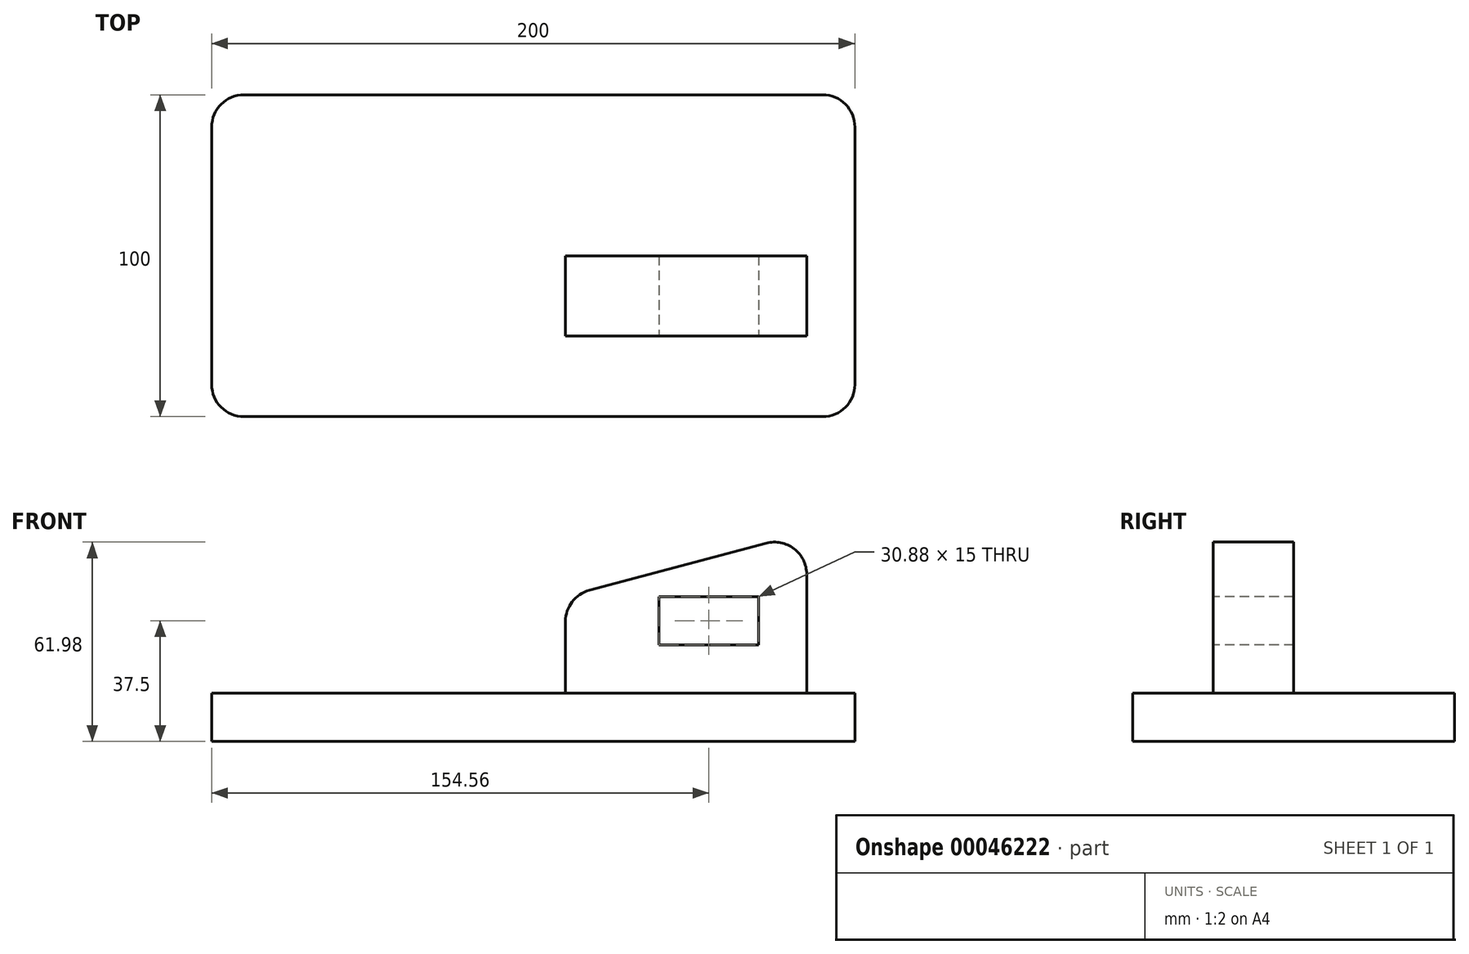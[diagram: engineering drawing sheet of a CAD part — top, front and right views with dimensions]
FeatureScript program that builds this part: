
annotation { "Feature Type Name" : "Feature", "Feature Type Description" : "" }
export const myFeature = defineFeature(function(context is Context, id is Id, definition is map)
    precondition{}
    {
        {
            var Q0;
            Q0=qCreatedBy(makeId("Top.planeOp"),FACE);
            var sketch = newSketch(context, id + "F0", { "sketchPlane" : qUnion([Q0])});
            skLineSegment(sketch, "E0.rect.bottom", {"start": v(100, 50) * mm, "end": v(-100, 50) * mm});
            skLineSegment(sketch, "E0.rect.top", {"start": v(100, -50) * mm, "end": v(-100, -50) * mm});
            skLineSegment(sketch, "E0.rect.left", {"start": v(100, 50) * mm, "end": v(100, -50) * mm});
            skLineSegment(sketch, "E0.rect.right", {"start": v(-100, 50) * mm, "end": v(-100, -50) * mm});
            skPoint(sketch, "E0.rect.middle", {"position": v(0, 0) * mm});
            skSolve(sketch);
        }
        {
            var Q0;
            Q0=makeQuery(id+"F0.imprint","IMPRINT",FACE,{"disambiguationData":[TD([[makeQuery(id+"F0.imprint","IMPRINT",EDGE,{"derivedFrom":sQuery(id+"F0.wireOp",EDGE,"E0.rect.bottom")}),1.0]])]});
            extrude(context, id + "F1", {"entities" : qUnion([Q0]), "depth" : 15 * mm});
        }
        {
            var Q0;
            Q0=makeQuery(id+"F1.opExtrude","SWEPT_FACE",FACE,{"disambiguationData":[OSD([sQuery(id+"F0.wireOp",EDGE,"E0.rect.top")])]});
            cPlane(context, id + "F2", {"entities" : qUnion([Q0]), "cplaneType" : CPlaneType.OFFSET, "offset" : 25 * mm, "oppositeDirection" : true, "width" : 150 * mm, "height" : 150 * mm});
        }
        {
            var Q0;
            Q0=qCreatedBy(id+"F2.planeOp",FACE);
            var sketch = newSketch(context, id + "F3", { "sketchPlane" : qUnion([Q0])});
            skLineSegment(sketch, "E1", {"start": v(85, 15) * mm, "end": v(85, 65) * mm});
            skLineSegment(sketch, "E2", {"start": v(85, 65) * mm, "end": v(10, 45) * mm});
            skLineSegment(sketch, "E3", {"start": v(10, 45) * mm, "end": v(10, 15) * mm});
            skLineSegment(sketch, "E4", {"start": v(10, 15) * mm, "end": v(85, 15) * mm});
            skLineSegment(sketch, "E5.bottom", {"start": v(70, 45) * mm, "end": v(39.12, 45) * mm});
            skLineSegment(sketch, "E5.top", {"start": v(70, 30) * mm, "end": v(39.12, 30) * mm});
            skLineSegment(sketch, "E5.left", {"start": v(70, 45) * mm, "end": v(70, 30) * mm});
            skLineSegment(sketch, "E5.right", {"start": v(39.12, 45) * mm, "end": v(39.12, 30) * mm});
            skSolve(sketch);
        }
        {
            var Q0;
            Q0 = qSketchRegion(id + "F3", true);
            extrude(context, id + "F4", {"entities" : qUnion([Q0]), "operationType" : NewBodyOperationType.ADD, "oppositeDirection" : true, "depth" : 25 * mm});
        }
        {
            var Q0;
            Q0=makeQuery(id+"F1.opExtrude","SWEPT_EDGE",EDGE,{"disambiguationData":[OSD([sQuery(id+"F0.wireOp",EDGE,"E0.rect.bottom"),sQuery(id+"F0.wireOp",EDGE,"E0.rect.right")])]});
            var Q1;
            Q1=makeQuery(id+"F1.opExtrude","SWEPT_EDGE",EDGE,{"disambiguationData":[OSD([sQuery(id+"F0.wireOp",EDGE,"E0.rect.top"),sQuery(id+"F0.wireOp",EDGE,"E0.rect.right")])]});
            var Q2;
            Q2=makeQuery(id+"F1.opExtrude","SWEPT_EDGE",EDGE,{"disambiguationData":[OSD([sQuery(id+"F0.wireOp",EDGE,"E0.rect.top"),sQuery(id+"F0.wireOp",EDGE,"E0.rect.left")])]});
            var Q3;
            Q3=makeQuery(id+"F1.opExtrude","SWEPT_EDGE",EDGE,{"disambiguationData":[OSD([sQuery(id+"F0.wireOp",EDGE,"E0.rect.bottom"),sQuery(id+"F0.wireOp",EDGE,"E0.rect.left")])]});
            var Q4;
            Q4=makeQuery(id+"F4.opExtrude","SWEPT_EDGE",EDGE,{"disambiguationData":[OSD([sQuery(id+"F3.wireOp",EDGE,"E2"),sQuery(id+"F3.wireOp",EDGE,"E3")])]});
            var Q5;
            Q5=makeQuery(id+"F4.opExtrude","SWEPT_EDGE",EDGE,{"disambiguationData":[OSD([sQuery(id+"F3.wireOp",EDGE,"E1"),sQuery(id+"F3.wireOp",EDGE,"E2")])]});
            fillet(context, id + "F5", {"entities" : qUnion([Q0, Q1, Q2, Q3, Q4, Q5]), "radius" : 10 * mm, "tangentPropagation" : true, "allowEdgeOverflow" : false});
        }
    });
